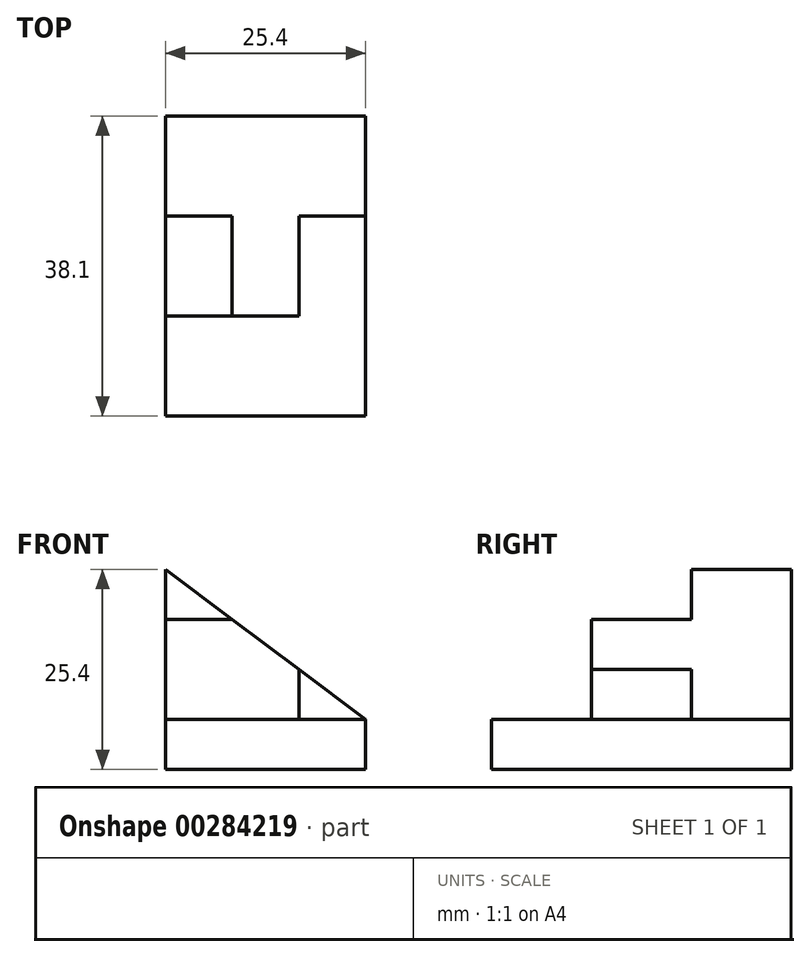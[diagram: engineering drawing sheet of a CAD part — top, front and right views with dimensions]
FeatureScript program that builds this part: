
annotation { "Feature Type Name" : "Feature", "Feature Type Description" : "" }
export const myFeature = defineFeature(function(context is Context, id is Id, definition is map)
    precondition{}
    {
        {
            var Q0;
            Q0=qCreatedBy(makeId("Front.planeOp"),FACE);
            var sketch = newSketch(context, id + "F0", { "sketchPlane" : qUnion([Q0])});
            skLineSegment(sketch, "E0", {"start": v(0, 0) * mm, "end": v(25.4, 0) * mm});
            skLineSegment(sketch, "E1", {"start": v(25.4, 0) * mm, "end": v(25.4, 6.35) * mm});
            skLineSegment(sketch, "E2", {"start": v(25.4, 6.35) * mm, "end": v(0, 6.35) * mm});
            skLineSegment(sketch, "E3", {"start": v(0, 6.35) * mm, "end": v(0, 0) * mm});
            skLineSegment(sketch, "E4", {"start": v(0, 6.35) * mm, "end": v(0, 25.4) * mm});
            skLineSegment(sketch, "E5", {"start": v(0, 25.4) * mm, "end": v(25.4, 6.35) * mm});
            skLineSegment(sketch, "E6", {"start": v(0, 19.05) * mm, "end": v(8.47, 19.05) * mm});
            skLineSegment(sketch, "E7", {"start": v(16.93, 12.7) * mm, "end": v(16.93, 6.35) * mm});
            skSolve(sketch);
        }
        {
            var Q0;
            Q0=makeQuery(id+"F0.imprint","IMPRINT",FACE,{"disambiguationData":[TD([[makeQuery(id+"F0.imprint","IMPRINT",EDGE,{"derivedFrom":sQuery(id+"F0.wireOp",EDGE,"E0")}),1.0]])]});
            extrude(context, id + "F1", {"entities" : qUnion([Q0]), "depth" : 38.1 * mm});
        }
        {
            var Q0;
            {var subQ0=sQuery(id+"F0.wireOp",EDGE,"E6");Q0=makeQuery(id+"F0.imprint","IMPRINT",FACE,{"disambiguationData":[TD([[makeQuery(id+"F0.imprint","IMPRINT",EDGE,{"derivedFrom":subQ0}),-1.0]])]});}
            extrude(context, id + "F2", {"entities" : qUnion([Q0]), "operationType" : NewBodyOperationType.ADD, "depth" : 25.4 * mm});
        }
        {
            var Q0;
            {var subQ3=sQuery(id+"F0.wireOp",EDGE,"E6");Q0=makeQuery(id+"F0.imprint","IMPRINT",FACE,{"disambiguationData":[TD([[makeQuery(id+"F0.imprint","IMPRINT",EDGE,{"derivedFrom":subQ3}),1.0]])]});}
            extrude(context, id + "F3", {"entities" : qUnion([Q0]), "operationType" : NewBodyOperationType.ADD, "depth" : 12.7 * mm});
        }
        {
            var Q0;
            {var subQ3=sQuery(id+"F0.wireOp",EDGE,"E7");Q0=makeQuery(id+"F0.imprint","IMPRINT",FACE,{"disambiguationData":[TD([[makeQuery(id+"F0.imprint","IMPRINT",EDGE,{"derivedFrom":subQ3}),1.0]])]});}
            extrude(context, id + "F4", {"entities" : qUnion([Q0]), "operationType" : NewBodyOperationType.ADD, "depth" : 12.7 * mm});
        }
    });
